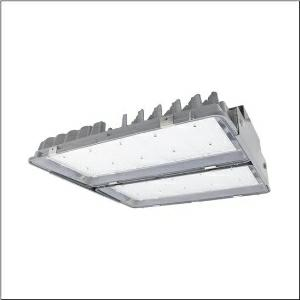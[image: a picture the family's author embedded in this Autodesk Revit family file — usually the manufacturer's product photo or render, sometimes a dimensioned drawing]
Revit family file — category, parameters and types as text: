
# Revit family: highbay_11xtreme_51hf61db4tma
name_source: partatom
category: Lighting Fixtures
units: mm (PartAtom-declared; Revit-internal decimal feet)

## family parameters
Cut with Voids When Loaded = No
Host = Face
Light Source = No
Part Type = Normal
Room Calculation Point = No
Round Connector Dimension = Use Diameter
Shared = No

## types (1)
- --- (1 x LED, 54000 lm, 282.6 W, 4000K)
    Apparent Load = 283 VA
    CIE Flux Codes = 88 96 99 100 100
    Color Rendering = 80
    Color Temperature = 4000K
    Default Elevation = 1800 mm
    Description = Highbay 11Xtreme, high bay luminaire, primary light control with lens, of PMMA, primary optical cover: cover, of toughened safety glass, light emission: direct distribution, primary light characteristic: symmetric, installation type: suspended mounting, surface-mounted, 2x LED module,for 1x 2x LED, rated luminous flux: 54.000lm, luminous efficacy: 191lm/W, light colour: 840, colour temperature: 4000K, control gear: DALI 2, with cable H07RN-F 5x 1.5mm², mains connection: 220..240V, AC, 50/60Hz, cable length: 1,5m, rated input power: 283W, luminaire housing, of diecast aluminium, coated, silver, length: 595mm, width: 560mm, height: 195mm, protection rating (complete): IP66, insulation class (complete): insulation class I (protective earthing), certification: CE, ENEC, UKCA, protection symbol: D, ball protection: ball impact resistant according to DIN VDE 0710 part 13 (with chain suspension), impact resistance: IK08, permissible operating ambient temperature: -25..+60°C, reducing of maximum allowable ambient temperature of 5°C with ceiling mounting, packaging unit: 1 piece
    Height = 157 mm
    Lamp = 1 x LED
    Lamp Light Flux = 54000 lm
    Lamp Power = 282.6 W
    Lamp count = 1
    Length = 593 mm
    Luminous efficacy = 191 lm/W
    Manufacturer = Siteco
    ModVariant = No
    Model = 51HF61DB4TMA
    Mounting Place = Ceiling
    Mounting Type = Pendant
    Number of Poles = 1
    OnlyDefault = Yes
    Power Factor = 1
    Product Name = Highbay 11Xtreme
    Product group = high bay luminaire
    ProductGroupID = 901
    Protection Class = Protection class I
    Protection Degree = IP 66
    RLX_Detail_Level = 1
    RLX_Emergency_Light_Flux = 0 lm
    RLX_Emergency_Type = 0
    RLX_Emergency_Type_DB = No
    RlxData = <blob elided: 33845 chars, md5=98cd8925>
    Socket = socket
    Standby Power = 0 W
    System Light Flux = 53999 lm
    System Power = 283 W
    Type Comments = factory setting: luminous flux: 100 % | dim-lin: 254 | 960 mA
    Type Image = l_1258340.jpg
    URL = http://relux.com
    VarID = @adj_083488
    Voltage = 0 V
    Weight = 0.00 kg
    Width = 278 mm

## geometry (parser evidence)
native form markers: Blend x4, Sweep x10
no freeform markers — native parametric forms only
